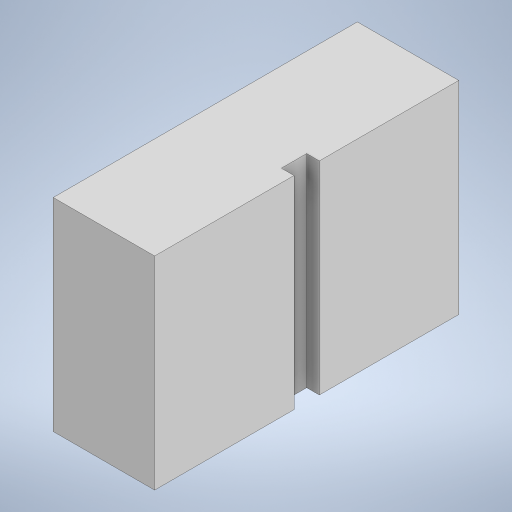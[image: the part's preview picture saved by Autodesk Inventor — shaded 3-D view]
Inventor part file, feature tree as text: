
AUTODESK INVENTOR PART (.ipt)
format: ipt  version: 2024 (Build 280153000, 153)  size: 191,488 bytes
history: native  units: in
note: dims shown in document units (in); Inventor stores cm internally (conversion verified against a paired STEP export)
features: extrude x2, sketch x2
ambient origin geometry x8: Origin, YZ Plane, XZ Plane, XY Plane, X Axis, Y Axis, Z Axis, Center Point
bodies: Solid1 (feature_tree)
feature tree (4):
  extrude  "Extrusion1"  Depth=3.1496in
  extrude  "Extrusion3"  Depth=0.3937in
  sketch  "Sketch1"  dims[d1=4.7244in d2=3.1496in]
  sketch  "Sketch5"  dims[d3=0.3937in d4=0.3937in d5=0.1969in d6=0.1969in d7=1.5748in d8=2.3622in d9=3.1496in d10=0.0in d13=1.5748in d14=0.0in d11=0.5in d12=0.0344in]
